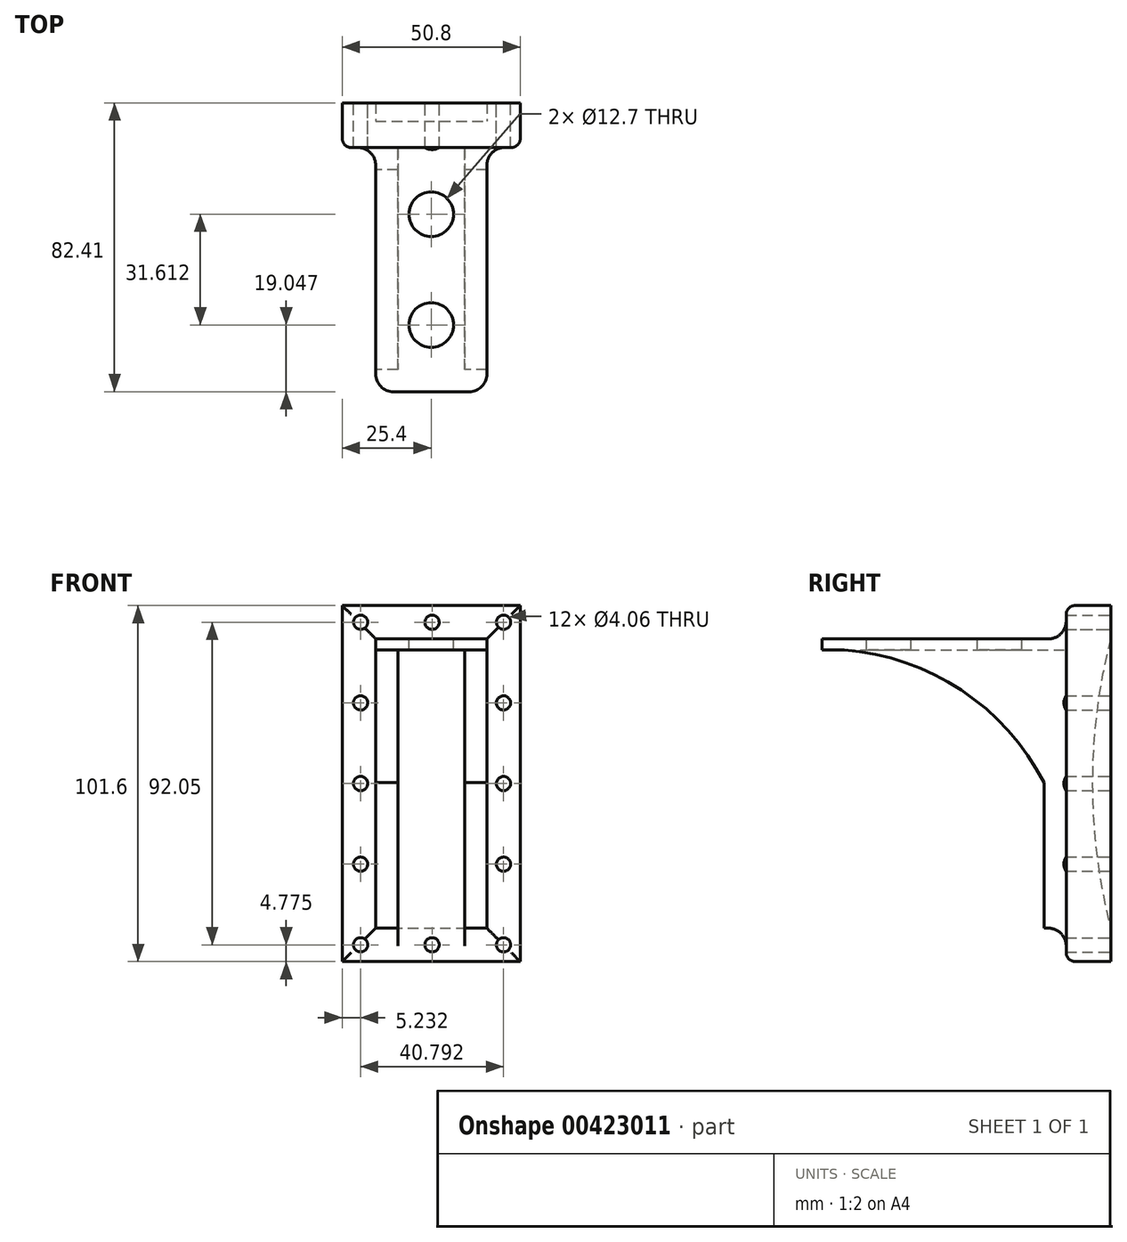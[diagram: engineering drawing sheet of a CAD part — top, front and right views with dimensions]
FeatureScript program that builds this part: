
annotation { "Feature Type Name" : "Feature", "Feature Type Description" : "" }
export const myFeature = defineFeature(function(context is Context, id is Id, definition is map)
    precondition{}
    {
        {
            var Q0;
            Q0=qCreatedBy(makeId("Front.planeOp"),FACE);
            var sketch = newSketch(context, id + "F0", { "sketchPlane" : qUnion([Q0])});
            skLineSegment(sketch, "E0.bottom", {"start": v(25.4, 50.8) * mm, "end": v(-25.4, 50.8) * mm});
            skLineSegment(sketch, "E0.top", {"start": v(25.4, -50.8) * mm, "end": v(-25.4, -50.8) * mm});
            skLineSegment(sketch, "E0.left", {"start": v(25.4, 50.8) * mm, "end": v(25.4, -50.8) * mm});
            skLineSegment(sketch, "E0.right", {"start": v(-25.4, 50.8) * mm, "end": v(-25.4, -50.8) * mm});
            skPoint(sketch, "E0.middle", {"position": v(0, 0) * mm});
            skSolve(sketch);
        }
        {
            var Q0;
            Q0=makeQuery(id+"F0.imprint","IMPRINT",FACE,{"disambiguationData":[TD([[makeQuery(id+"F0.imprint","IMPRINT",EDGE,{"derivedFrom":sQuery(id+"F0.wireOp",EDGE,"E0.bottom")}),1.0]])]});
            var sketch = newSketch(context, id + "F1", { "sketchPlane" : qUnion([Q0])});
            skLineSegment(sketch, "E1.bottom", {"start": v(15.88, 41.28) * mm, "end": v(-15.88, 41.28) * mm});
            skLineSegment(sketch, "E1.top", {"start": v(15.88, -41.28) * mm, "end": v(-15.88, -41.28) * mm});
            skLineSegment(sketch, "E1.left", {"start": v(15.88, 41.28) * mm, "end": v(15.88, -41.28) * mm});
            skLineSegment(sketch, "E1.right", {"start": v(-15.88, 41.28) * mm, "end": v(-15.88, -41.28) * mm});
            skPoint(sketch, "E1.middle", {"position": v(0, 0) * mm});
            skSolve(sketch);
        }
        {
            var Q0;
            Q0=makeQuery(id+"F0.imprint","IMPRINT",FACE,{"disambiguationData":[TD([[makeQuery(id+"F0.imprint","IMPRINT",EDGE,{"derivedFrom":sQuery(id+"F0.wireOp",EDGE,"E0.bottom")}),1.0]])]});
            extrude(context, id + "F2", {"entities" : qUnion([Q0]), "depth" : 12.7 * mm});
        }
        {
            var Q0;
            Q0 = qSketchRegion(id + "F1", true);
            extrude(context, id + "F3", {"entities" : qUnion([Q0]), "operationType" : NewBodyOperationType.ADD, "depth" : 19.05 * mm});
        }
        {
            var Q0;
            Q0=qCreatedBy(makeId("Right.planeOp"),FACE);
            var sketch = newSketch(context, id + "F4", { "sketchPlane" : qUnion([Q0])});
            skLineSegment(sketch, "E2", {"start": v(-18.91, 38.1) * mm, "end": v(-76.06, 38.1) * mm});
            skLineSegment(sketch, "E3", {"start": v(-18.91, 38.1) * mm, "end": v(-18.91, 0) * mm});
            skArc(sketch, "E4", {"start": v(-18.91, 0) * mm, "mid": v(-42.48, 26.56) * mm, "end": v(-76.06, 38.1) * mm});
            skLineSegment(sketch, "E5.bottom", {"start": v(-18.91, 38.1) * mm, "end": v(-82.41, 38.1) * mm});
            skLineSegment(sketch, "E5.top", {"start": v(-18.91, 41.28) * mm, "end": v(-82.41, 41.28) * mm});
            skLineSegment(sketch, "E5.left", {"start": v(-18.91, 38.1) * mm, "end": v(-18.91, 41.28) * mm});
            skLineSegment(sketch, "E5.right", {"start": v(-82.41, 38.1) * mm, "end": v(-82.41, 41.28) * mm});
            skLineSegment(sketch, "E6.bottom", {"start": v(-76.06, 38.1) * mm, "end": v(-82.41, 38.1) * mm});
            skLineSegment(sketch, "E6.top", {"start": v(-76.06, 38.1) * mm, "end": v(-82.41, 38.1) * mm});
            skLineSegment(sketch, "E6.left", {"start": v(-82.41, 38.1) * mm, "end": v(-82.41, 38.1) * mm});
            skLineSegment(sketch, "E6.right", {"start": v(-76.06, 38.1) * mm, "end": v(-76.06, 38.1) * mm});
            skSolve(sketch);
        }
        {
            var Q0;
            Q0 = qSketchRegion(id + "F4", true);
            extrude(context, id + "F5", {"entities" : qUnion([Q0]), "operationType" : NewBodyOperationType.ADD, "depth" : 15.88 * mm, "hasSecondDirection" : true, "secondDirectionOppositeDirection" : true, "secondDirectionDepth" : 15.88 * mm});
        }
        {
            var Q0;
            Q0=qCreatedBy(makeId("Right.planeOp"),FACE);
            var sketch = newSketch(context, id + "F6", { "sketchPlane" : qUnion([Q0])});
            skLineSegment(sketch, "E7.bottom", {"start": v(-88.83, 38.1) * mm, "end": v(-12.7, 38.1) * mm});
            skLineSegment(sketch, "E7.top", {"start": v(-88.83, -46.62) * mm, "end": v(-12.7, -46.62) * mm});
            skLineSegment(sketch, "E7.left", {"start": v(-88.83, 38.1) * mm, "end": v(-88.83, -46.62) * mm});
            skLineSegment(sketch, "E7.right", {"start": v(-12.7, 38.1) * mm, "end": v(-12.7, -46.62) * mm});
            skSolve(sketch);
        }
        {
            var Q0;
            Q0 = qSketchRegion(id + "F6", true);
            extrude(context, id + "F7", {"entities" : qUnion([Q0]), "operationType" : NewBodyOperationType.REMOVE, "oppositeDirection" : true, "depth" : 9.52 * mm, "hasSecondDirection" : true, "secondDirectionOppositeDirection" : false, "secondDirectionDepth" : 9.52 * mm});
        }
        {
            var Q0;
            Q0=makeQuery(id+"F5.opExtrude","SWEPT_FACE",FACE,{"disambiguationData":[OSD([sQuery(id+"F4.wireOp",EDGE,"E5.top")])]});
            var sketch = newSketch(context, id + "F8", { "sketchPlane" : qUnion([Q0])});
            skPoint(sketch, "E8", {"position": v(0, -63.36) * mm});
            skPoint(sketch, "E9", {"position": v(0, -31.75) * mm});
            skSolve(sketch);
        }
        {
            var Q0;
            Q0=sQuery(id+"F8.wireOp",VERTEX,"E9");
            var Q1;
            Q1=sQuery(id+"F8.wireOp",VERTEX,"E8");
            var Q2;
            Q2=makeQuery(id+"F2.opExtrude","SWEPT_BODY",BODY,{"disambiguationData":[OSD([sQuery(id+"F0.wireOp",EDGE,"E0.bottom"),sQuery(id+"F0.wireOp",EDGE,"E0.top"),sQuery(id+"F0.wireOp",EDGE,"E0.left"),sQuery(id+"F0.wireOp",EDGE,"E0.right")])]});
            hole(context, id + "F9", {"style" : HoleStyle.C_BORE, "endStyle" : HoleEndStyle.THROUGH, "holeDiameter" : 12.7 * mm, "cBoreDiameter" : 12.7 * mm, "cBoreDepth" : 0 * mm, "isTappedThrough" : true, "tappedDepth" : 12.7 * mm, "tapClearance" : 3, "locations" : qUnion([Q0, Q1]), "scope" : qUnion([Q2])});
        }
        {
            var Q0;
            Q0=makeQuery(id+"F5.opExtrude","CAP_EDGE",EDGE,{"disambiguationData":[OSD([sQuery(id+"F4.wireOp",EDGE,"E5.right")])],"isStart":true});
            var Q1;
            Q1=makeQuery(id+"F5.opExtrude","CAP_EDGE",EDGE,{"disambiguationData":[OSD([sQuery(id+"F4.wireOp",EDGE,"E5.right")])],"isStart":false});
            var Q2;
            Q2=makeQuery(id+"F3.boolean.opBoolean","INTERSECT",EDGE,{"derivedFrom":[makeQuery(id+"F2.opExtrude","CAP_FACE",FACE,{"disambiguationData":[OSD([sQuery(id+"F0.wireOp",EDGE,"E0.bottom"),sQuery(id+"F0.wireOp",EDGE,"E0.top"),sQuery(id+"F0.wireOp",EDGE,"E0.left"),sQuery(id+"F0.wireOp",EDGE,"E0.right")])],"isStart":false}),makeQuery(id+"F3.opExtrude","SWEPT_FACE",FACE,{"disambiguationData":[OSD([sQuery(id+"F1.wireOp",EDGE,"E1.right")])]})]});
            var Q3;
            Q3=makeQuery(id+"F3.boolean.opBoolean","INTERSECT",EDGE,{"derivedFrom":[makeQuery(id+"F2.opExtrude","CAP_FACE",FACE,{"disambiguationData":[OSD([sQuery(id+"F0.wireOp",EDGE,"E0.bottom"),sQuery(id+"F0.wireOp",EDGE,"E0.top"),sQuery(id+"F0.wireOp",EDGE,"E0.left"),sQuery(id+"F0.wireOp",EDGE,"E0.right")])],"isStart":false}),makeQuery(id+"F3.opExtrude","SWEPT_FACE",FACE,{"disambiguationData":[OSD([sQuery(id+"F1.wireOp",EDGE,"E1.left")])]})]});
            var Q4;
            Q4=makeQuery(id+"F3.boolean.opBoolean","INTERSECT",EDGE,{"derivedFrom":[makeQuery(id+"F2.opExtrude","CAP_FACE",FACE,{"disambiguationData":[OSD([sQuery(id+"F0.wireOp",EDGE,"E0.bottom"),sQuery(id+"F0.wireOp",EDGE,"E0.top"),sQuery(id+"F0.wireOp",EDGE,"E0.left"),sQuery(id+"F0.wireOp",EDGE,"E0.right")])],"isStart":false}),makeQuery(id+"F3.opExtrude","SWEPT_FACE",FACE,{"disambiguationData":[OSD([sQuery(id+"F1.wireOp",EDGE,"E1.bottom")])]})]});
            var Q5;
            {var subQ1=makeQuery(id+"F3.opExtrude","SWEPT_FACE",FACE,{"disambiguationData":[OSD([sQuery(id+"F1.wireOp",EDGE,"E1.top")])]});var subQ2=makeQuery(id+"F2.opExtrude","CAP_FACE",FACE,{"disambiguationData":[OSD([sQuery(id+"F0.wireOp",EDGE,"E0.bottom"),sQuery(id+"F0.wireOp",EDGE,"E0.top"),sQuery(id+"F0.wireOp",EDGE,"E0.left"),sQuery(id+"F0.wireOp",EDGE,"E0.right")])],"isStart":false});Q5=makeQuery(id+"F7.boolean.opBoolean","SPLIT",EDGE,{"disambiguationData":[topologyDisambiguationEdgeConnected([subQ2,subQ1]),TD([makeQuery(id+"F3.opExtrude","SWEPT_FACE",FACE,{"disambiguationData":[OSD([sQuery(id+"F1.wireOp",EDGE,"E1.left")])]})])],"derivedFrom":makeQuery(id+"F3.boolean.opBoolean","INTERSECT",EDGE,{"derivedFrom":[subQ2,subQ1]})});}
            var Q6;
            {var subQ0=makeQuery(id+"F3.opExtrude","SWEPT_FACE",FACE,{"disambiguationData":[OSD([sQuery(id+"F1.wireOp",EDGE,"E1.top")])]});var subQ1=makeQuery(id+"F2.opExtrude","CAP_FACE",FACE,{"disambiguationData":[OSD([sQuery(id+"F0.wireOp",EDGE,"E0.bottom"),sQuery(id+"F0.wireOp",EDGE,"E0.top"),sQuery(id+"F0.wireOp",EDGE,"E0.left"),sQuery(id+"F0.wireOp",EDGE,"E0.right")])],"isStart":false});Q6=makeQuery(id+"F7.boolean.opBoolean","SPLIT",EDGE,{"disambiguationData":[topologyDisambiguationEdgeConnected([subQ1,subQ0]),TD([makeQuery(id+"F3.opExtrude","SWEPT_FACE",FACE,{"disambiguationData":[OSD([sQuery(id+"F1.wireOp",EDGE,"E1.right")])]})])],"derivedFrom":makeQuery(id+"F3.boolean.opBoolean","INTERSECT",EDGE,{"derivedFrom":[subQ1,subQ0]})});}
            fillet(context, id + "F10", {"entities" : qUnion([Q0, Q1, Q2, Q3, Q4, Q5, Q6]), "radius" : 5.08 * mm, "tangentPropagation" : true, "allowEdgeOverflow" : false});
        }
        {
            var Q0;
            Q0=makeQuery(id+"F2.opExtrude","CAP_FACE",FACE,{"disambiguationData":[OSD([sQuery(id+"F0.wireOp",EDGE,"E0.bottom"),sQuery(id+"F0.wireOp",EDGE,"E0.top"),sQuery(id+"F0.wireOp",EDGE,"E0.left"),sQuery(id+"F0.wireOp",EDGE,"E0.right")])],"isStart":true});
            var sketch = newSketch(context, id + "F11", { "sketchPlane" : qUnion([Q0])});
            skPoint(sketch, "E10", {"position": v(-20.62, 46.02) * mm});
            skPoint(sketch, "E11", {"position": v(-0.23, 46.02) * mm});
            skPoint(sketch, "E12", {"position": v(20.17, 46.02) * mm});
            skPoint(sketch, "E13", {"position": v(-20.62, 23.01) * mm});
            skPoint(sketch, "E14", {"position": v(-20.62, 0) * mm});
            skPoint(sketch, "E15", {"position": v(-20.62, -23.01) * mm});
            skPoint(sketch, "E16", {"position": v(-20.62, -46.02) * mm});
            skPoint(sketch, "E17", {"position": v(20.17, 23.01) * mm});
            skPoint(sketch, "E18", {"position": v(20.17, 0) * mm});
            skPoint(sketch, "E19", {"position": v(20.17, -23.01) * mm});
            skPoint(sketch, "E20", {"position": v(20.17, -46.02) * mm});
            skPoint(sketch, "E21", {"position": v(-0.23, -46.02) * mm});
            skSolve(sketch);
        }
        {
            var Q0;
            Q0=sQuery(id+"F11.wireOp",VERTEX,"E10");
            var Q1;
            Q1=sQuery(id+"F11.wireOp",VERTEX,"E11");
            var Q2;
            Q2=sQuery(id+"F11.wireOp",VERTEX,"E12");
            var Q3;
            Q3=sQuery(id+"F11.wireOp",VERTEX,"E17");
            var Q4;
            Q4=sQuery(id+"F11.wireOp",VERTEX,"E18");
            var Q5;
            Q5=sQuery(id+"F11.wireOp",VERTEX,"E19");
            var Q6;
            Q6=sQuery(id+"F11.wireOp",VERTEX,"E20");
            var Q7;
            Q7=sQuery(id+"F11.wireOp",VERTEX,"E21");
            var Q8;
            Q8=sQuery(id+"F11.wireOp",VERTEX,"E16");
            var Q9;
            Q9=sQuery(id+"F11.wireOp",VERTEX,"E15");
            var Q10;
            Q10=sQuery(id+"F11.wireOp",VERTEX,"E14");
            var Q11;
            Q11=sQuery(id+"F11.wireOp",VERTEX,"E13");
            var Q12;
            Q12=makeQuery(id+"F2.opExtrude","SWEPT_BODY",BODY,{"disambiguationData":[OSD([sQuery(id+"F0.wireOp",EDGE,"E0.bottom"),sQuery(id+"F0.wireOp",EDGE,"E0.top"),sQuery(id+"F0.wireOp",EDGE,"E0.left"),sQuery(id+"F0.wireOp",EDGE,"E0.right")])]});
            hole(context, id + "F12", {"style" : HoleStyle.C_BORE, "endStyle" : HoleEndStyle.THROUGH, "holeDiameter" : 4.06 * mm, "cBoreDiameter" : 4.06 * mm, "cBoreDepth" : 0 * mm, "isTappedThrough" : true, "tappedDepth" : 12.7 * mm, "tapClearance" : 3, "locations" : qUnion([Q0, Q1, Q2, Q3, Q4, Q5, Q6, Q7, Q8, Q9, Q10, Q11]), "scope" : qUnion([Q12])});
        }
        {
            var Q0;
            Q0=makeQuery(id+"F2.opExtrude","CAP_EDGE",EDGE,{"disambiguationData":[OSD([sQuery(id+"F0.wireOp",EDGE,"E0.bottom")])],"isStart":false});
            var Q1;
            Q1=makeQuery(id+"F2.opExtrude","CAP_EDGE",EDGE,{"disambiguationData":[OSD([sQuery(id+"F0.wireOp",EDGE,"E0.right")])],"isStart":false});
            var Q2;
            Q2=makeQuery(id+"F2.opExtrude","CAP_EDGE",EDGE,{"disambiguationData":[OSD([sQuery(id+"F0.wireOp",EDGE,"E0.top")])],"isStart":false});
            var Q3;
            Q3=makeQuery(id+"F2.opExtrude","CAP_EDGE",EDGE,{"disambiguationData":[OSD([sQuery(id+"F0.wireOp",EDGE,"E0.left")])],"isStart":false});
            fillet(context, id + "F13", {"entities" : qUnion([Q0, Q1, Q2, Q3]), "radius" : 2.54 * mm, "tangentPropagation" : true, "allowEdgeOverflow" : false});
        }
        {
            var Q0;
            Q0=qCreatedBy(makeId("Right.planeOp"),FACE);
            var sketch = newSketch(context, id + "F14", { "sketchPlane" : qUnion([Q0])});
            skArc(sketch, "E22", {"start": v(0, 41.27) * mm, "mid": v(-5.24, 0) * mm, "end": v(0, -41.28) * mm});
            skLineSegment(sketch, "E23", {"start": v(0, 41.27) * mm, "end": v(0, -41.27) * mm});
            skSolve(sketch);
        }
        {
            var Q0;
            Q0 = qSketchRegion(id + "F14", true);
            extrude(context, id + "F15", {"entities" : qUnion([Q0]), "operationType" : NewBodyOperationType.REMOVE, "oppositeDirection" : true, "depth" : 15.88 * mm, "hasSecondDirection" : true, "secondDirectionOppositeDirection" : false, "secondDirectionDepth" : 15.88 * mm});
        }
    });
